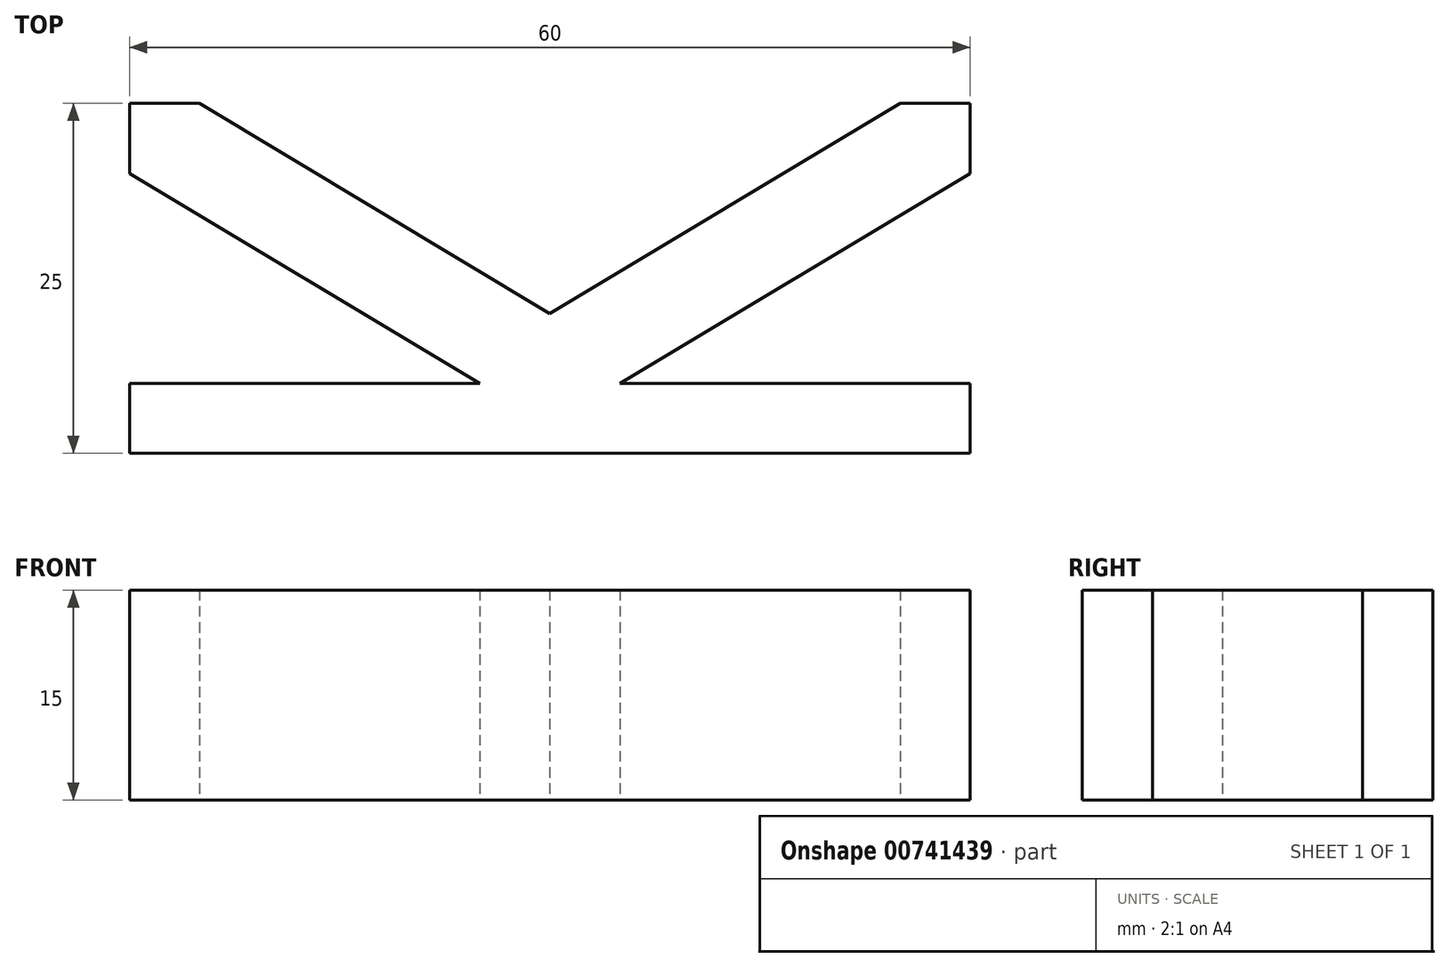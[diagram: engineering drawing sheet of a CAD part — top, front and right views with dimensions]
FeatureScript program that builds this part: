
annotation { "Feature Type Name" : "Feature", "Feature Type Description" : "" }
export const myFeature = defineFeature(function(context is Context, id is Id, definition is map)
    precondition{}
    {
        {
            var Q0;
            Q0=qCreatedBy(makeId("Top.planeOp"),FACE);
            var sketch = newSketch(context, id + "F0", { "sketchPlane" : qUnion([Q0])});
            skLineSegment(sketch, "E0", {"start": v(0, 0) * mm, "end": v(0, 5) * mm});
            skLineSegment(sketch, "E1", {"start": v(0, 5) * mm, "end": v(25, 20) * mm});
            skLineSegment(sketch, "E2", {"start": v(25, 20) * mm, "end": v(30, 20) * mm});
            skLineSegment(sketch, "E3", {"start": v(30, 20) * mm, "end": v(30, 15) * mm});
            skLineSegment(sketch, "E4", {"start": v(30, 15) * mm, "end": v(5, 0) * mm});
            skLineSegment(sketch, "E5", {"start": v(5, 0) * mm, "end": v(0, 0) * mm});
            skLineSegment(sketch, "E6.MirrorCS", {"start": v(-30, 20) * mm, "end": v(-30, 15) * mm});
            skLineSegment(sketch, "E7.MirrorCS", {"start": v(-25, 20) * mm, "end": v(-30, 20) * mm});
            skLineSegment(sketch, "E8.MirrorCS", {"start": v(0, 5) * mm, "end": v(-25, 20) * mm});
            skLineSegment(sketch, "E9.MirrorCS", {"start": v(-5, 0) * mm, "end": v(0, 0) * mm});
            skLineSegment(sketch, "E10.MirrorCS", {"start": v(-30, 15) * mm, "end": v(-5, 0) * mm});
            skLineSegment(sketch, "E11.bottom", {"start": v(-30, 0) * mm, "end": v(30, 0) * mm});
            skLineSegment(sketch, "E11.top", {"start": v(-30, -5) * mm, "end": v(30, -5) * mm});
            skLineSegment(sketch, "E11.left", {"start": v(-30, 0) * mm, "end": v(-30, -5) * mm});
            skLineSegment(sketch, "E11.right", {"start": v(30, 0) * mm, "end": v(30, -5) * mm});
            skSolve(sketch);
        }
        {
            var Q0;
            Q0 = qSketchRegion(id + "F0", true);
            extrude(context, id + "F1", {"entities" : qUnion([Q0]), "depth" : 15 * mm, "offsetDistance" : 25 * mm});
        }
    });
